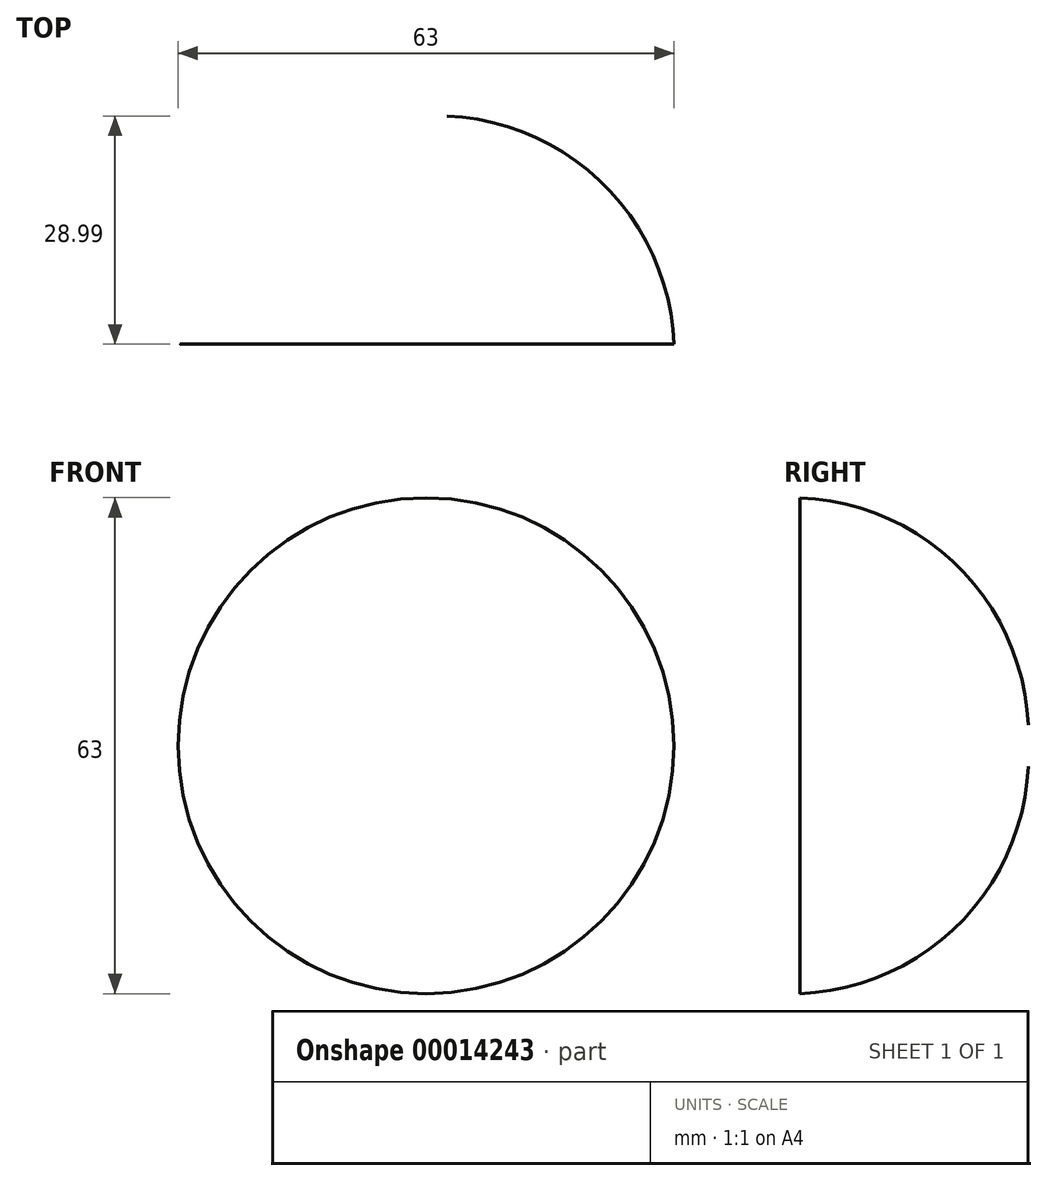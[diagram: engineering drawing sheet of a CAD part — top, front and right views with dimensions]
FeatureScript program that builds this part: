
annotation { "Feature Type Name" : "Feature", "Feature Type Description" : "" }
export const myFeature = defineFeature(function(context is Context, id is Id, definition is map)
    precondition{}
    {
        {
            var Q0;
            Q0=qCreatedBy(makeId("Top.planeOp"),FACE);
            var sketch = newSketch(context, id + "F0", { "sketchPlane" : qUnion([Q0])});
            skArc(sketch, "E0", {"start": v(0, -31.33) * mm, "mid": v(22.62, -22.57) * mm, "end": v(31.5, 0) * mm});
            skLineSegment(sketch, "E1", {"start": v(0, -31.33) * mm, "end": v(0, 0) * mm});
            skLineSegment(sketch, "E2", {"start": v(0, 0) * mm, "end": v(31.5, 0) * mm});
            skSolve(sketch);
        }
        {
            var Q0;
            Q0=makeQuery(id+"F0.imprint","IMPRINT",FACE,{"disambiguationData":[TD([[makeQuery(id+"F0.imprint","IMPRINT",EDGE,{"derivedFrom":sQuery(id+"F0.wireOp",EDGE,"E0")}),1.0]])]});
            var Q1;
            Q1=sQuery(id+"F0.wireOp",EDGE,"E1");
            revolve(context, id + "F1", {"entities" : qUnion([Q0]), "axis" : qUnion([Q1]), "revolveType" : RevolveType.FULL});
        }
    });
